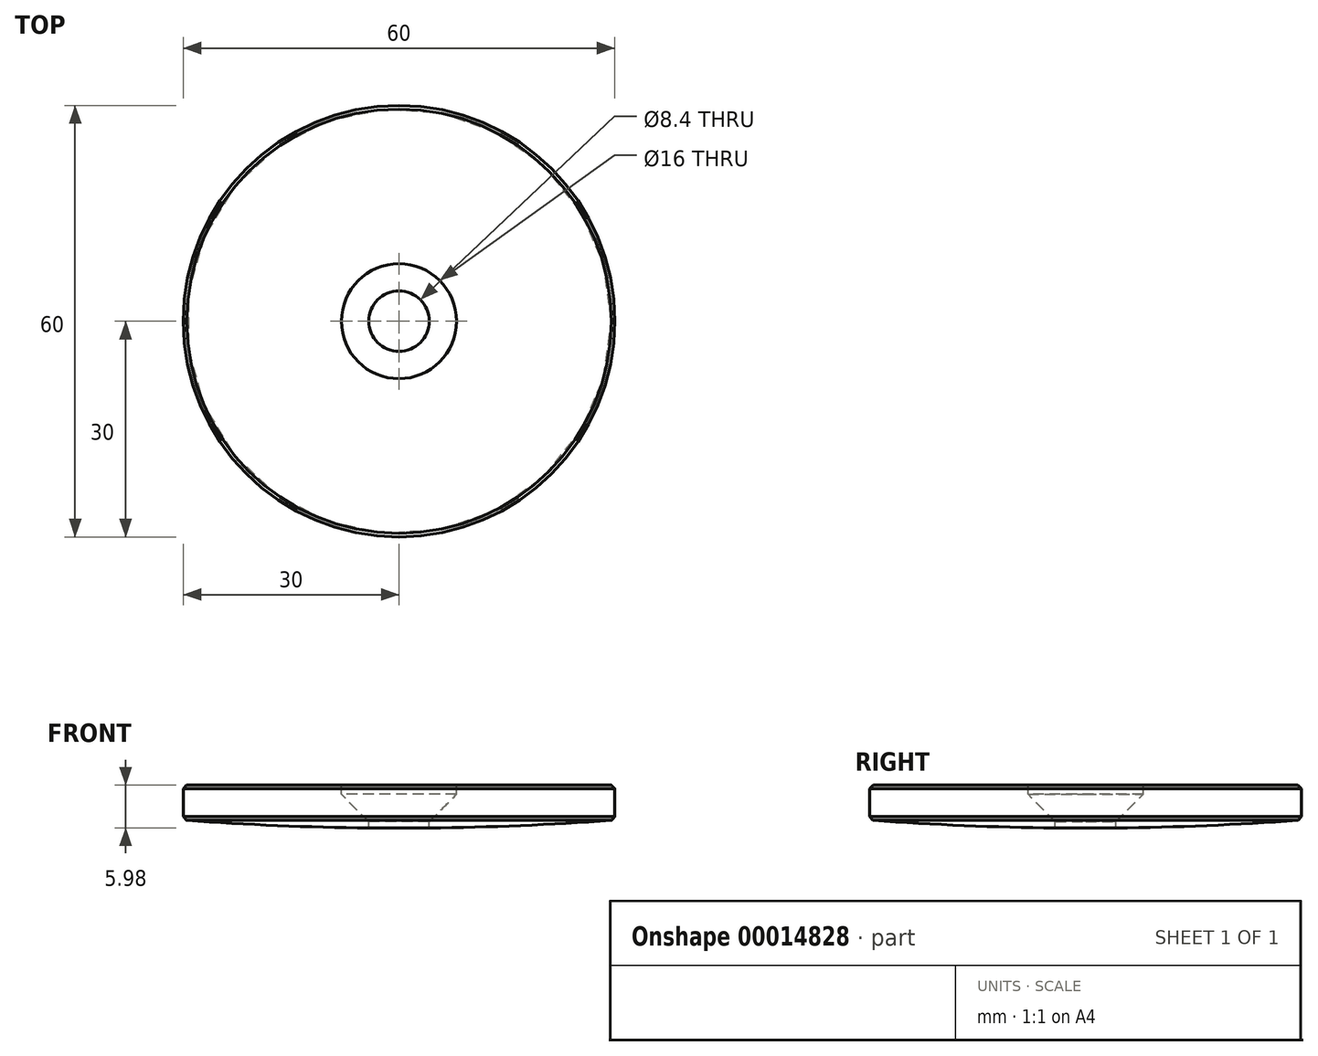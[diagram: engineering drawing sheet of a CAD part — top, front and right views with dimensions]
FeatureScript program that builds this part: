
annotation { "Feature Type Name" : "Feature", "Feature Type Description" : "" }
export const myFeature = defineFeature(function(context is Context, id is Id, definition is map)
    precondition{}
    {
        {
            var Q0;
            Q0=qCreatedBy(makeId("Top.planeOp"),FACE);
            var sketch = newSketch(context, id + "F0", { "sketchPlane" : qUnion([Q0])});
            skCircle(sketch, "E0", {"center": v(0, 0) * mm, "radius": 30 * mm});
            skSolve(sketch);
        }
        {
            var Q0;
            Q0 = qSketchRegion(id + "F0", true);
            extrude(context, id + "F1", {"entities" : qUnion([Q0]), "depth" : 6 * mm});
        }
        {
            var Q0;
            Q0=makeQuery(id+"F1.opExtrude","CAP_FACE",FACE,{"disambiguationData":[OSD([sQuery(id+"F0.wireOp",EDGE,"E0")])],"isStart":false});
            var sketch = newSketch(context, id + "F2", { "sketchPlane" : qUnion([Q0])});
            skCircle(sketch, "E1", {"center": v(0, 0) * mm, "radius": 8 * mm});
            skCircle(sketch, "E2", {"center": v(0, 0) * mm, "radius": 4.2 * mm});
            skSolve(sketch);
        }
        {
            var Q0;
            Q0=makeQuery(id+"F2.imprint","IMPRINT",FACE,{"disambiguationData":[TD([[makeQuery(id+"F2.imprint","IMPRINT",EDGE,{"derivedFrom":sQuery(id+"F2.wireOp",EDGE,"E2")}),1.0]])]});
            extrude(context, id + "F3", {"entities" : qUnion([Q0]), "operationType" : NewBodyOperationType.REMOVE, "endBound" : BoundingType.THROUGH_ALL, "oppositeDirection" : true, "depth" : 25 * mm});
        }
        {
            var Q0;
            Q0=makeQuery(id+"F2.imprint","IMPRINT",FACE,{"disambiguationData":[TD([[makeQuery(id+"F2.imprint","IMPRINT",EDGE,{"derivedFrom":sQuery(id+"F2.wireOp",EDGE,"E1")}),1.0]])]});
            extrude(context, id + "F4", {"entities" : qUnion([Q0]), "operationType" : NewBodyOperationType.REMOVE, "oppositeDirection" : true, "depth" : 5.8 * mm});
        }
        {
            var Q0;
            Q0=qCreatedBy(makeId("Front.planeOp"),FACE);
            var sketch = newSketch(context, id + "F5", { "sketchPlane" : qUnion([Q0])});
            skArc(sketch, "E3", {"start": v(-400, 382) * mm, "mid": v(0, 0) * mm, "end": v(400, 382) * mm, "construction": true});
            skLineSegment(sketch, "E4", {"start": v(0, 400.42) * mm, "end": v(0, 0) * mm, "construction": true});
            skLineSegment(sketch, "E5", {"start": v(-400, 382) * mm, "end": v(400, 382) * mm, "construction": true});
            skSolve(sketch);
        }
        {
            var Q0;
            Q0=makeQuery(id+"F1.opExtrude","CAP_FACE",FACE,{"disambiguationData":[OSD([sQuery(id+"F0.wireOp",EDGE,"E0")])],"isStart":true});
            cPlane(context, id + "F6", {"entities" : qUnion([Q0]), "cplaneType" : CPlaneType.OFFSET, "offset" : 382 * mm, "oppositeDirection" : true, "width" : 150 * mm, "height" : 150 * mm});
        }
        {
            var Q0;
            Q0=qCreatedBy(id+"F6.planeOp",FACE);
            var sketch = newSketch(context, id + "F7", { "sketchPlane" : qUnion([Q0])});
            skArc(sketch, "E6", {"start": v(-396.86, 50) * mm, "mid": v(-400, 0) * mm, "end": v(-396.86, -50) * mm});
            skLineSegment(sketch, "E7", {"start": v(-396.86, -50) * mm, "end": v(-450, -50) * mm});
            skLineSegment(sketch, "E8", {"start": v(-450, -50) * mm, "end": v(-450, 50) * mm});
            skLineSegment(sketch, "E9", {"start": v(-450, 50) * mm, "end": v(-396.86, 50) * mm});
            skSolve(sketch);
        }
        {
            var Q0;
            Q0 = qSketchRegion(id + "F7", true);
            var Q1;
            Q1=sQuery(id+"F5.wireOp",EDGE,"E3");
            revolve(context, id + "F8", {"operationType" : NewBodyOperationType.REMOVE, "entities" : qUnion([Q0]), "axis" : qUnion([Q1]), "revolveType" : RevolveType.FULL, "oppositeDirection" : true});
        }
        {
            var Q0;
            Q0=makeQuery(id+"F4.boolean.opBoolean","COPY",EDGE,{"derivedFrom":makeQuery(id+"F4.opExtrude","CAP_EDGE",EDGE,{"disambiguationData":[OSD([sQuery(id+"F2.wireOp",EDGE,"E1")])],"isStart":false})});
            chamfer(context, id + "F9", {"entities" : qUnion([Q0]), "chamferType" : ChamferType.OFFSET_ANGLE, "width" : 4.5 * mm, "oppositeDirection" : false, "angle" : 45 * degree, "tangentPropagation" : true});
        }
        {
            var Q0;
            Q0=makeQuery(id+"F1.opExtrude","CAP_EDGE",EDGE,{"disambiguationData":[OSD([sQuery(id+"F0.wireOp",EDGE,"E0")])],"isStart":false});
            var Q1;
            Q1=makeQuery(id+"F4.boolean.opBoolean","COPY",EDGE,{"derivedFrom":makeQuery(id+"F4.opExtrude","CAP_EDGE",EDGE,{"disambiguationData":[OSD([sQuery(id+"F2.wireOp",EDGE,"E1")])],"isStart":true})});
            var Q2;
            Q2=makeQuery(id+"F8.boolean.opBoolean","INTERSECT",EDGE,{"derivedFrom":[makeQuery(id+"F1.opExtrude","SWEPT_FACE",FACE,{"disambiguationData":[OSD([sQuery(id+"F0.wireOp",EDGE,"E0")])]}),makeQuery(id+"F8.opRevolve","SWEPT_FACE",FACE,{"disambiguationData":[OSD([sQuery(id+"F7.wireOp",EDGE,"E6")])]})]});
            chamfer(context, id + "F10", {"entities" : qUnion([Q0, Q1, Q2]), "width" : .5 * mm, "tangentPropagation" : true});
        }
    });
